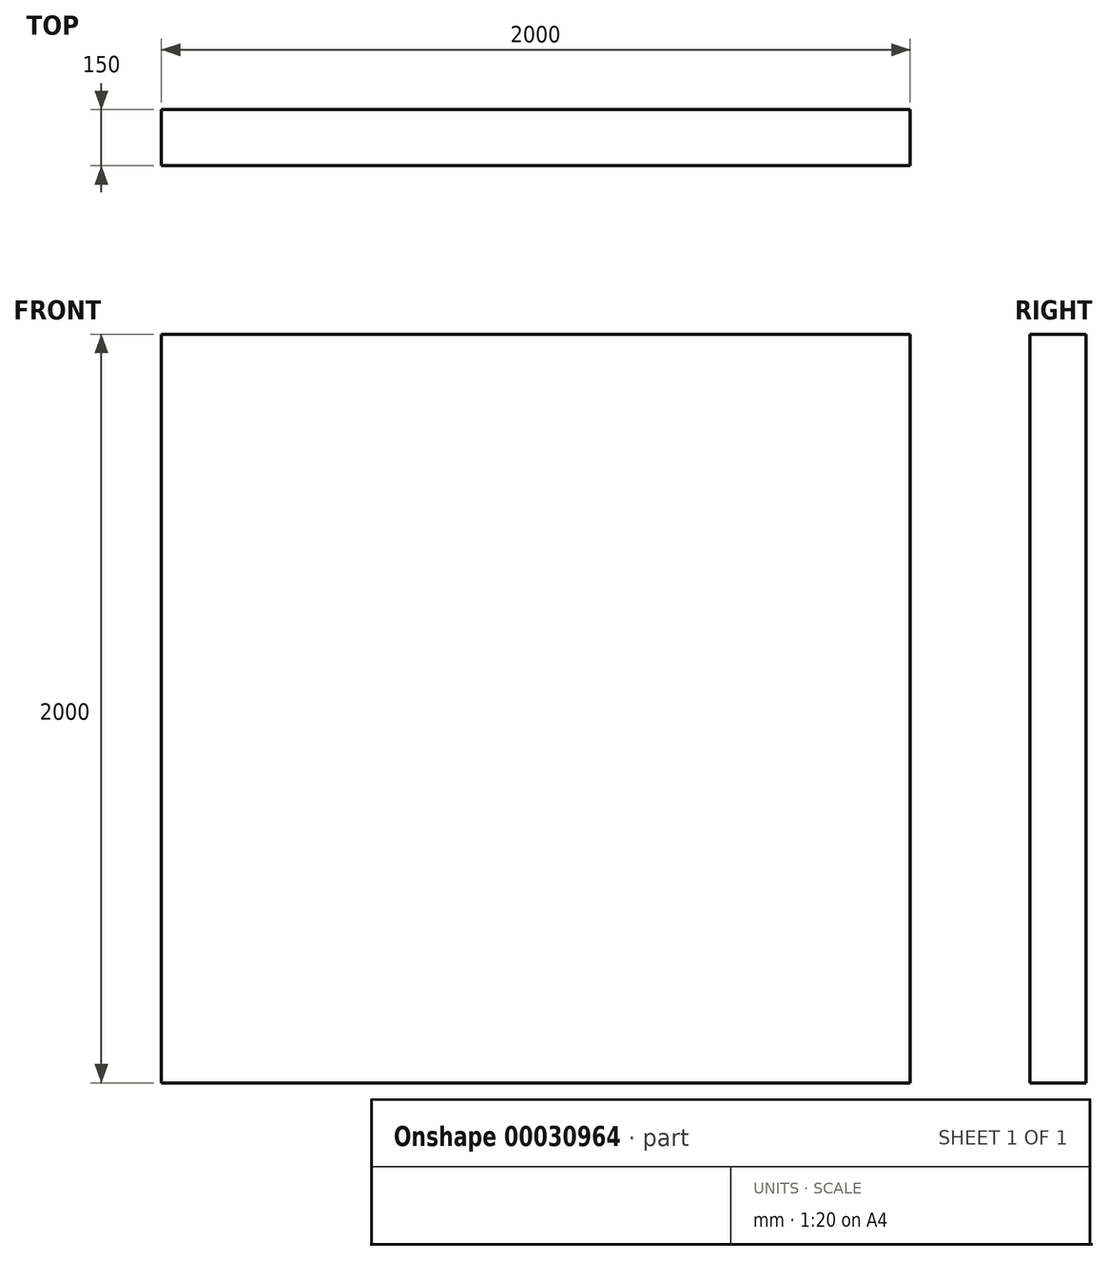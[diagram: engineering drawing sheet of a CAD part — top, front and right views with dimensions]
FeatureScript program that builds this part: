
annotation { "Feature Type Name" : "Feature", "Feature Type Description" : "" }
export const myFeature = defineFeature(function(context is Context, id is Id, definition is map)
    precondition{}
    {
        {
            var Q0;
            Q0=qCreatedBy(makeId("Front.planeOp"),FACE);
            var sketch = newSketch(context, id + "F0", { "sketchPlane" : qUnion([Q0])});
            skLineSegment(sketch, "E0.rect.bottom", {"start": v(-1000, 1000) * mm, "end": v(1000, 1000) * mm});
            skLineSegment(sketch, "E0.rect.top", {"start": v(-1000, -1000) * mm, "end": v(1000, -1000) * mm});
            skLineSegment(sketch, "E0.rect.left", {"start": v(-1000, 1000) * mm, "end": v(-1000, -1000) * mm});
            skLineSegment(sketch, "E0.rect.right", {"start": v(1000, 1000) * mm, "end": v(1000, -1000) * mm});
            skPoint(sketch, "E0.rect.middle", {"position": v(0, 0) * mm});
            skSolve(sketch);
        }
        {
            var Q0;
            Q0 = qSketchRegion(id + "F0", true);
            extrude(context, id + "F1", {"entities" : qUnion([Q0]), "depth" : 150 * mm});
        }
    });
